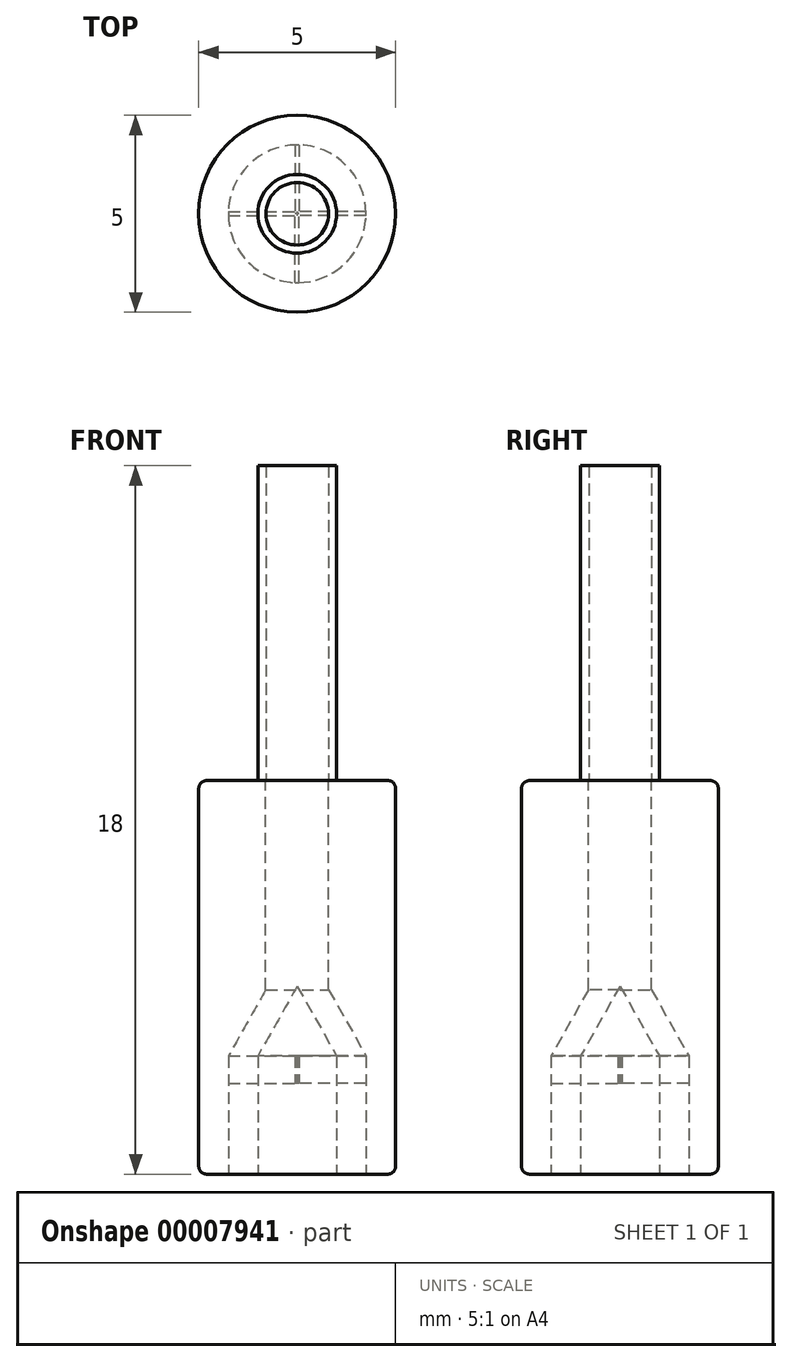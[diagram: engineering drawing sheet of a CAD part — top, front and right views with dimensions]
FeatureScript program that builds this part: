
annotation { "Feature Type Name" : "Feature", "Feature Type Description" : "" }
export const myFeature = defineFeature(function(context is Context, id is Id, definition is map)
    precondition{}
    {
        {
            var Q0;
            Q0=qCreatedBy(makeId("Top.planeOp"),FACE);
            var sketch = newSketch(context, id + "F0", { "sketchPlane" : qUnion([Q0])});
            skCircle(sketch, "E0", {"center": v(0, 0) * mm, "radius": 2.5 * mm});
            skSolve(sketch);
        }
        {
            var Q0;
            Q0=makeQuery(id+"F0.imprint","IMPRINT",FACE,{"disambiguationData":[TD([[makeQuery(id+"F0.imprint","IMPRINT",EDGE,{"derivedFrom":sQuery(id+"F0.wireOp",EDGE,"E0")}),1.0]])]});
            extrude(context, id + "F1", {"entities" : qUnion([Q0]), "depth" : 10 * mm});
        }
        {
            var Q0;
            Q0=makeQuery(id+"F1.opExtrude","CAP_FACE",FACE,{"disambiguationData":[OSD([sQuery(id+"F0.wireOp",EDGE,"E0")])],"isStart":false});
            var sketch = newSketch(context, id + "F2", { "sketchPlane" : qUnion([Q0])});
            skCircle(sketch, "E1", {"center": v(0, 0) * mm, "radius": 0.8 * mm});
            skCircle(sketch, "E2", {"center": v(0, 0) * mm, "radius": 1 * mm});
            skSolve(sketch);
        }
        {
            var Q0;
            Q0=makeQuery(id+"F2.imprint","IMPRINT",FACE,{"disambiguationData":[TD([[makeQuery(id+"F2.imprint","IMPRINT",EDGE,{"derivedFrom":sQuery(id+"F2.wireOp",EDGE,"E1")}),-1.0]])]});
            extrude(context, id + "F3", {"entities" : qUnion([Q0]), "operationType" : NewBodyOperationType.ADD, "depth" : 8 * mm});
        }
        {
            var Q0;
            Q0=makeQuery(id+"F1.opExtrude","CAP_FACE",FACE,{"disambiguationData":[OSD([sQuery(id+"F0.wireOp",EDGE,"E0")])],"isStart":true});
            var sketch = newSketch(context, id + "F4", { "sketchPlane" : qUnion([Q0])});
            skCircle(sketch, "E3", {"center": v(0, 0) * mm, "radius": 1 * mm});
            skCircle(sketch, "E4", {"center": v(0, 0) * mm, "radius": 1.75 * mm});
            skSolve(sketch);
        }
        {
            var Q0;
            Q0=makeQuery(id+"F4.imprint","IMPRINT",FACE,{"disambiguationData":[TD([[makeQuery(id+"F4.imprint","IMPRINT",EDGE,{"derivedFrom":sQuery(id+"F4.wireOp",EDGE,"E3")}),-1.0]])]});
            extrude(context, id + "F5", {"entities" : qUnion([Q0]), "operationType" : NewBodyOperationType.REMOVE, "oppositeDirection" : true, "depth" : 3 * mm});
        }
        {
            var Q0;
            Q0=qCreatedBy(makeId("Front.planeOp"),FACE);
            var sketch = newSketch(context, id + "F6", { "sketchPlane" : qUnion([Q0])});
            skLineSegment(sketch, "E5", {"start": v(-1.75, 3) * mm, "end": v(0, 6.1) * mm});
            skLineSegment(sketch, "E6", {"start": v(0, 4.77) * mm, "end": v(-1, 3) * mm});
            skLineSegment(sketch, "E7", {"start": v(-1, 3) * mm, "end": v(-1.75, 3) * mm});
            skLineSegment(sketch, "E8", {"start": v(0, 6.1) * mm, "end": v(0, 4.77) * mm});
            skLineSegment(sketch, "E9", {"start": v(0, 0) * mm, "end": v(0, 3.06) * mm});
            skSolve(sketch);
        }
        {
            var Q0;
            Q0 = qSketchRegion(id + "F6", true);
            var Q1;
            Q1=sQuery(id+"F6.wireOp",EDGE,"E9");
            revolve(context, id + "F7", {"operationType" : NewBodyOperationType.REMOVE, "entities" : qUnion([Q0]), "axis" : qUnion([Q1]), "revolveType" : RevolveType.ONE_DIRECTION, "oppositeDirection" : true, "angle" : 360 * degree});
        }
        {
            var Q0;
            Q0=qCreatedBy(makeId("Front.planeOp"),FACE);
            var sketch = newSketch(context, id + "F8", { "sketchPlane" : qUnion([Q0])});
            skLineSegment(sketch, "E10.bottom", {"start": v(-0.05, 3) * mm, "end": v(0.05, 3) * mm});
            skLineSegment(sketch, "E10.top", {"start": v(-0.05, 2.3) * mm, "end": v(0.05, 2.3) * mm});
            skLineSegment(sketch, "E10.left", {"start": v(-0.05, 3) * mm, "end": v(-0.05, 2.3) * mm});
            skLineSegment(sketch, "E10.right", {"start": v(0.05, 3) * mm, "end": v(0.05, 2.3) * mm});
            skSolve(sketch);
        }
        {
            var Q0;
            Q0 = qSketchRegion(id + "F8", true);
            var Q1;
            Q1=makeQuery(id+"F1.opExtrude","SWEPT_FACE",FACE,{"disambiguationData":[OSD([sQuery(id+"F0.wireOp",EDGE,"E0")])]});
            extrude(context, id + "F9", {"entities" : qUnion([Q0]), "endBound" : BoundingType.UP_TO_BODY, "endBoundEntityBody" : qUnion([Q1]), "depth" : 25 * mm});
        }
        {
            var Q0;
            Q0=makeQuery(id+"F9.opExtrude","SWEPT_BODY",BODY,{"disambiguationData":[OSD([sQuery(id+"F8.wireOp",EDGE,"E10.bottom"),sQuery(id+"F8.wireOp",EDGE,"E10.top"),sQuery(id+"F8.wireOp",EDGE,"E10.left"),sQuery(id+"F8.wireOp",EDGE,"E10.right")])]});
            var Q1;
            Q1=makeQuery(id+"F5.boolean.opBoolean","COPY",EDGE,{"derivedFrom":makeQuery(id+"F5.opExtrude","CAP_EDGE",EDGE,{"disambiguationData":[OSD([sQuery(id+"F4.wireOp",EDGE,"E3")])],"isStart":true})});
            circularPattern(context, id + "F10", {"entities" : qUnion([Q0]), "axis" : qUnion([Q1]), "angle" : 90 * degree, "instanceCount" : 4});
        }
        {
            var Q0;
            Q0=qCreatedBy(makeId("Right.planeOp"),FACE);
            var sketch = newSketch(context, id + "F11", { "sketchPlane" : qUnion([Q0])});
            skLineSegment(sketch, "E11", {"start": v(-0.8, 10) * mm, "end": v(-0.8, 4.68) * mm});
            skLineSegment(sketch, "E12", {"start": v(-0.8, 4.68) * mm, "end": v(0, 6) * mm});
            skLineSegment(sketch, "E13", {"start": v(-0.8, 10) * mm, "end": v(0, 10) * mm});
            skLineSegment(sketch, "E14", {"start": v(0, 10) * mm, "end": v(0, 6) * mm});
            skSolve(sketch);
        }
        {
            var Q0;
            Q0=makeQuery(id+"F11.imprint","IMPRINT",FACE,{"disambiguationData":[TD([[makeQuery(id+"F11.imprint","IMPRINT",EDGE,{"derivedFrom":sQuery(id+"F11.wireOp",EDGE,"E11")}),1.0]])]});
            var Q1;
            Q1=sQuery(id+"F11.wireOp",EDGE,"E14");
            revolve(context, id + "F12", {"operationType" : NewBodyOperationType.REMOVE, "entities" : qUnion([Q0]), "axis" : qUnion([Q1]), "revolveType" : RevolveType.ONE_DIRECTION, "angle" : 360 * degree});
        }
        {
            var Q0;
            Q0=makeQuery(id+"F1.opExtrude","CAP_EDGE",EDGE,{"disambiguationData":[OSD([sQuery(id+"F0.wireOp",EDGE,"E0")])],"isStart":true});
            var Q1;
            Q1=makeQuery(id+"F1.opExtrude","CAP_EDGE",EDGE,{"disambiguationData":[OSD([sQuery(id+"F0.wireOp",EDGE,"E0")])],"isStart":false});
            fillet(context, id + "F13", {"entities" : qUnion([Q0, Q1]), "radius" : 0.2 * mm, "tangentPropagation" : true, "allowEdgeOverflow" : false});
        }
    });
